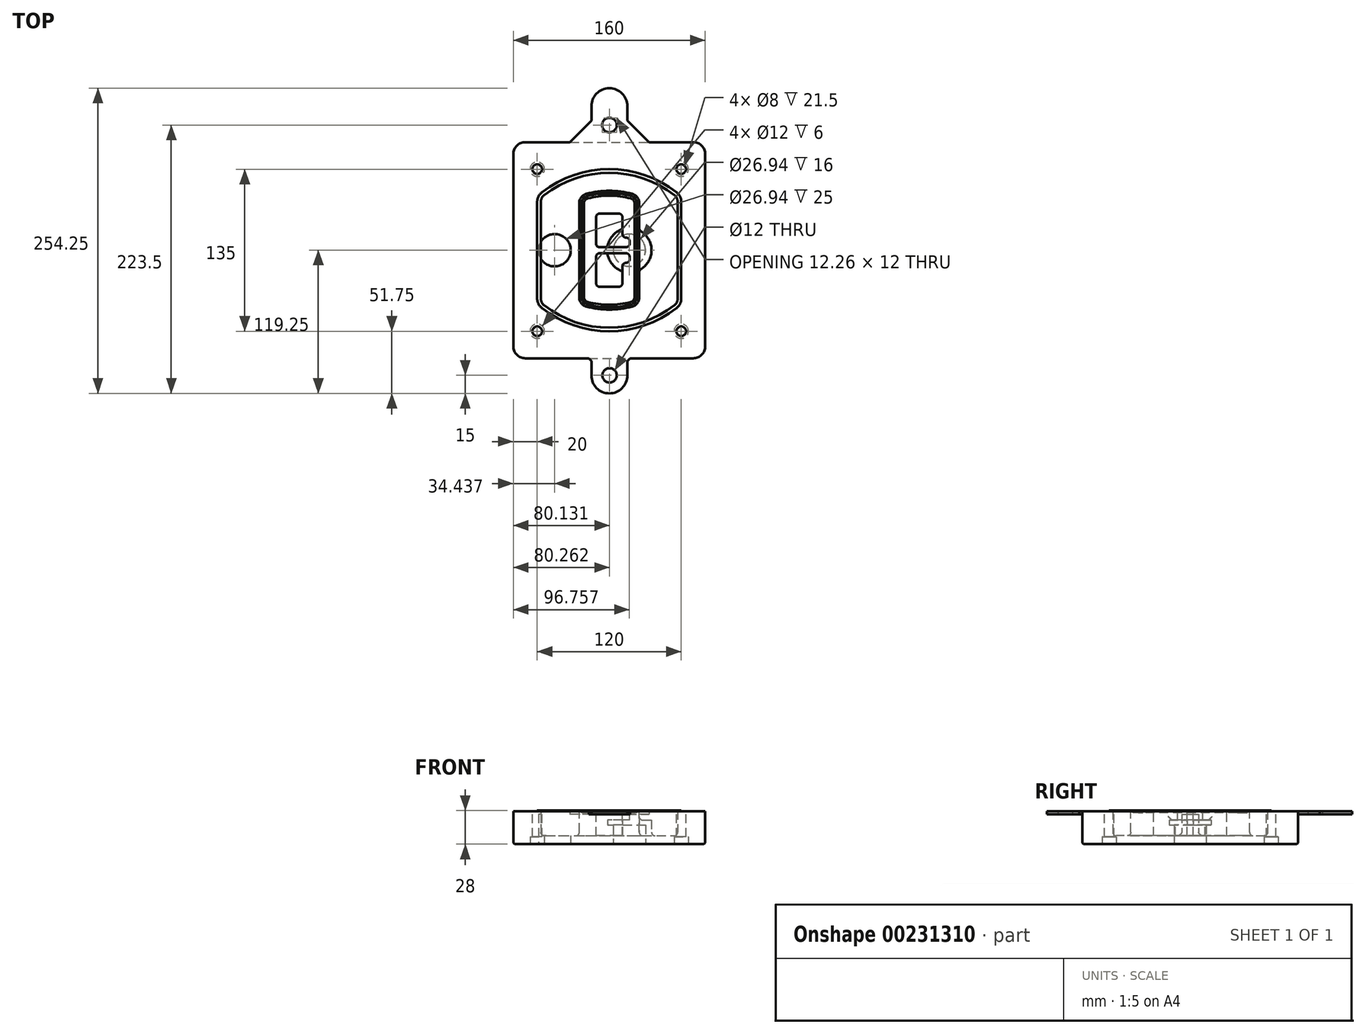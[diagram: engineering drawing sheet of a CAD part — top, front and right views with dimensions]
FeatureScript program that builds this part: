
annotation { "Feature Type Name" : "Feature", "Feature Type Description" : "" }
export const myFeature = defineFeature(function(context is Context, id is Id, definition is map)
    precondition{}
    {
        {
            var Q0;
            Q0=qCreatedBy(makeId("Top.planeOp"),FACE);
            var sketch = newSketch(context, id + "F0", { "sketchPlane" : qUnion([Q0])});
            skPoint(sketch, "E0.rect.middle", {"position": v(0, 0) * mm});
            skLineSegment(sketch, "E1.bottom", {"start": v(-70, -90) * mm, "end": v(70, -90) * mm});
            skLineSegment(sketch, "E1.top", {"start": v(-70, 90) * mm, "end": v(70, 90) * mm});
            skLineSegment(sketch, "E1.left", {"start": v(-80, -80) * mm, "end": v(-80, 80) * mm});
            skLineSegment(sketch, "E1.right", {"start": v(80, -80) * mm, "end": v(80, 80) * mm});
            skLineSegment(sketch, "E2", {"start": v(-80, 90) * mm, "end": v(80, -90) * mm, "construction": true});
            skLineSegment(sketch, "E3", {"start": v(80, 90) * mm, "end": v(-80, -90) * mm, "construction": true});
            skCircle(sketch, "E4", {"center": v(-60, 67.5) * mm, "radius": 4 * mm});
            skCircle(sketch, "E5", {"center": v(60, 67.5) * mm, "radius": 4 * mm});
            skCircle(sketch, "E6", {"center": v(60, -67.5) * mm, "radius": 4 * mm});
            skCircle(sketch, "E7", {"center": v(-60, -67.5) * mm, "radius": 4 * mm});
            skLineSegment(sketch, "E8", {"start": v(-60, 67.5) * mm, "end": v(60, 67.5) * mm, "construction": true});
            skLineSegment(sketch, "E9", {"start": v(60, 67.5) * mm, "end": v(60, -67.5) * mm, "construction": true});
            skLineSegment(sketch, "E10", {"start": v(60, -67.5) * mm, "end": v(-60, -67.5) * mm, "construction": true});
            skLineSegment(sketch, "E11", {"start": v(-60, -67.5) * mm, "end": v(-60, 67.5) * mm, "construction": true});
            skLineSegment(sketch, "E12", {"start": v(-60, 40.3) * mm, "end": v(-60, -40.3) * mm});
            skLineSegment(sketch, "E13", {"start": v(60, 40.3) * mm, "end": v(60, -40.3) * mm});
            skArc(sketch, "E14", {"start": v(56.15, 48.18) * mm, "mid": v(0, 67.5) * mm, "end": v(-56.15, 48.18) * mm});
            skArc(sketch, "E15", {"start": v(-56.15, -48.18) * mm, "mid": v(0, -67.5) * mm, "end": v(56.15, -48.18) * mm});
            skLineSegment(sketch, "E16", {"start": v(-60, 0) * mm, "end": v(60, 0) * mm, "construction": true});
            skPoint(sketch, "E17.visualSharp", {"position": v(-60, -45) * mm});
            skArc(sketch, "E17.filletArc", {"start": v(-60, -40.3) * mm, "mid": v(-58.99, -44.68) * mm, "end": v(-56.15, -48.18) * mm});
            skPoint(sketch, "E18.visualSharp", {"position": v(-60, 45) * mm});
            skArc(sketch, "E18.filletArc", {"start": v(-56.15, 48.18) * mm, "mid": v(-58.99, 44.68) * mm, "end": v(-60, 40.3) * mm});
            skPoint(sketch, "E19.visualSharp", {"position": v(60, 45) * mm});
            skArc(sketch, "E19.filletArc", {"start": v(60, 40.3) * mm, "mid": v(58.99, 44.68) * mm, "end": v(56.15, 48.18) * mm});
            skPoint(sketch, "E20.visualSharp", {"position": v(60, -45) * mm});
            skArc(sketch, "E20.filletArc", {"start": v(56.15, -48.18) * mm, "mid": v(58.99, -44.68) * mm, "end": v(60, -40.3) * mm});
            skPoint(sketch, "E21.visualSharp", {"position": v(-80, 90) * mm});
            skArc(sketch, "E21.filletArc", {"start": v(-70, 90) * mm, "mid": v(-77.07, 87.07) * mm, "end": v(-80, 80) * mm});
            skPoint(sketch, "E22.visualSharp", {"position": v(80, 90) * mm});
            skArc(sketch, "E22.filletArc", {"start": v(80, 80) * mm, "mid": v(77.07, 87.07) * mm, "end": v(70, 90) * mm});
            skPoint(sketch, "E23.visualSharp", {"position": v(80, -90) * mm});
            skArc(sketch, "E23.filletArc", {"start": v(70, -90) * mm, "mid": v(77.07, -87.07) * mm, "end": v(80, -80) * mm});
            skPoint(sketch, "E24.visualSharp", {"position": v(-80, -90) * mm});
            skArc(sketch, "E24.filletArc", {"start": v(-80, -80) * mm, "mid": v(-77.07, -87.07) * mm, "end": v(-70, -90) * mm});
            skArc(sketch, "E25.0", {"start": v(57, 40.3) * mm, "mid": v(56.3, 43.36) * mm, "end": v(54.3, 45.81) * mm});
            skLineSegment(sketch, "E25.1", {"start": v(57, 40.3) * mm, "end": v(57, -40.3) * mm});
            skArc(sketch, "E25.2", {"start": v(54.3, -45.81) * mm, "mid": v(56.3, -43.36) * mm, "end": v(57, -40.3) * mm});
            skArc(sketch, "E25.3", {"start": v(-54.3, -45.81) * mm, "mid": v(0, -64.5) * mm, "end": v(54.3, -45.81) * mm});
            skArc(sketch, "E25.4", {"start": v(-57, -40.3) * mm, "mid": v(-56.3, -43.36) * mm, "end": v(-54.3, -45.81) * mm});
            skArc(sketch, "E25.5", {"start": v(54.3, 45.81) * mm, "mid": v(0, 64.5) * mm, "end": v(-54.3, 45.81) * mm});
            skLineSegment(sketch, "E25.6", {"start": v(-57, 40.3) * mm, "end": v(-57, -40.3) * mm});
            skArc(sketch, "E25.7", {"start": v(-54.3, 45.81) * mm, "mid": v(-56.3, 43.36) * mm, "end": v(-57, 40.3) * mm});
            skArc(sketch, "E26.0", {"start": v(-58.62, 51.33) * mm, "mid": v(-62.58, 46.43) * mm, "end": v(-64, 40.3) * mm});
            skArc(sketch, "E26.1", {"start": v(58.62, 51.33) * mm, "mid": v(0, 71.5) * mm, "end": v(-58.62, 51.33) * mm});
            skArc(sketch, "E26.2", {"start": v(64, 40.3) * mm, "mid": v(62.58, 46.43) * mm, "end": v(58.62, 51.33) * mm});
            skLineSegment(sketch, "E26.3", {"start": v(64, 40.3) * mm, "end": v(64, -40.3) * mm});
            skArc(sketch, "E26.4", {"start": v(58.62, -51.33) * mm, "mid": v(62.58, -46.43) * mm, "end": v(64, -40.3) * mm});
            skLineSegment(sketch, "E26.5", {"start": v(-64, 40.3) * mm, "end": v(-64, -40.3) * mm});
            skArc(sketch, "E26.6", {"start": v(-58.62, -51.33) * mm, "mid": v(0, -71.5) * mm, "end": v(58.62, -51.33) * mm});
            skArc(sketch, "E26.7", {"start": v(-64, -40.3) * mm, "mid": v(-62.58, -46.43) * mm, "end": v(-58.62, -51.33) * mm});
            skSolve(sketch);
        }
        {
            var Q0;
            Q0=makeQuery(id+"F0.imprint","IMPRINT",FACE,{"disambiguationData":[TD([[makeQuery(id+"F0.imprint","IMPRINT",EDGE,{"derivedFrom":sQuery(id+"F0.wireOp",EDGE,"E1.bottom")}),1.0]])]});
            var Q1;
            Q1=makeQuery(id+"F0.imprint","IMPRINT",FACE,{"disambiguationData":[TD([[makeQuery(id+"F0.imprint","IMPRINT",EDGE,{"derivedFrom":sQuery(id+"F0.wireOp",EDGE,"E12")}),1.0]])]});
            var Q2;
            Q2=makeQuery(id+"F0.imprint","IMPRINT",FACE,{"disambiguationData":[TD([[makeQuery(id+"F0.imprint","IMPRINT",EDGE,{"derivedFrom":sQuery(id+"F0.wireOp",EDGE,"E25.0")}),1.0]])]});
            var Q3;
            Q3=makeQuery(id+"F0.imprint","IMPRINT",FACE,{"disambiguationData":[TD([[makeQuery(id+"F0.imprint","IMPRINT",EDGE,{"derivedFrom":sQuery(id+"F0.wireOp",EDGE,"E12")}),-1.0]])]});
            extrude(context, id + "F1", {"entities" : qUnion([Q0, Q1, Q2, Q3]), "oppositeDirection" : true, "depth" : 25 * mm});
        }
        {
            var Q0;
            Q0=makeQuery(id+"F0.imprint","IMPRINT",FACE,{"disambiguationData":[TD([[makeQuery(id+"F0.imprint","IMPRINT",EDGE,{"derivedFrom":sQuery(id+"F0.wireOp",EDGE,"E12")}),1.0]])]});
            extrude(context, id + "F2", {"entities" : qUnion([Q0]), "operationType" : NewBodyOperationType.ADD, "depth" : 3 * mm});
        }
        {
            var Q0;
            Q0=makeQuery(id+"F0.imprint","IMPRINT",FACE,{"disambiguationData":[TD([[makeQuery(id+"F0.imprint","IMPRINT",EDGE,{"derivedFrom":sQuery(id+"F0.wireOp",EDGE,"E25.0")}),1.0]])]});
            extrude(context, id + "F3", {"entities" : qUnion([Q0]), "operationType" : NewBodyOperationType.REMOVE, "oppositeDirection" : true, "depth" : 18 * mm});
        }
        {
            var Q0;
            Q0=makeQuery(id+"F2.opExtrude","CAP_FACE",FACE,{"disambiguationData":[OSD([sQuery(id+"F0.wireOp",EDGE,"E12"),sQuery(id+"F0.wireOp",EDGE,"E13"),sQuery(id+"F0.wireOp",EDGE,"E14"),sQuery(id+"F0.wireOp",EDGE,"E15"),sQuery(id+"F0.wireOp",EDGE,"E17.filletArc"),sQuery(id+"F0.wireOp",EDGE,"E18.filletArc"),sQuery(id+"F0.wireOp",EDGE,"E19.filletArc"),sQuery(id+"F0.wireOp",EDGE,"E20.filletArc"),sQuery(id+"F0.wireOp",EDGE,"E25.0"),sQuery(id+"F0.wireOp",EDGE,"E25.1"),sQuery(id+"F0.wireOp",EDGE,"E25.2"),sQuery(id+"F0.wireOp",EDGE,"E25.3"),sQuery(id+"F0.wireOp",EDGE,"E25.4"),sQuery(id+"F0.wireOp",EDGE,"E25.5"),sQuery(id+"F0.wireOp",EDGE,"E25.6"),sQuery(id+"F0.wireOp",EDGE,"E25.7")])],"isStart":false});
            var sketch = newSketch(context, id + "F4", { "sketchPlane" : qUnion([Q0])});
            skArc(sketch, "E27.0", {"start": v(-19.08, -46.97) * mm, "mid": v(0, -49.5) * mm, "end": v(19.08, -46.97) * mm});
            skArc(sketch, "E28.0", {"start": v(19.08, 46.97) * mm, "mid": v(0, 49.5) * mm, "end": v(-19.08, 46.97) * mm});
            skLineSegment(sketch, "E29", {"start": v(-25, 39.25) * mm, "end": v(-25, -39.25) * mm});
            skLineSegment(sketch, "E30", {"start": v(25, 39.25) * mm, "end": v(25, -39.25) * mm});
            skLineSegment(sketch, "E31", {"start": v(-25, 45.1) * mm, "end": v(25, 45.1) * mm, "construction": true});
            skLineSegment(sketch, "E32", {"start": v(-25, -45.1) * mm, "end": v(25, -45.1) * mm, "construction": true});
            skPoint(sketch, "E33.visualSharp", {"position": v(-25, 45.1) * mm});
            skArc(sketch, "E33.filletArc", {"start": v(-19.08, 46.97) * mm, "mid": v(-23.35, 44.11) * mm, "end": v(-25, 39.25) * mm});
            skPoint(sketch, "E34.visualSharp", {"position": v(25, 45.1) * mm});
            skArc(sketch, "E34.filletArc", {"start": v(25, 39.25) * mm, "mid": v(23.35, 44.11) * mm, "end": v(19.08, 46.97) * mm});
            skPoint(sketch, "E35.visualSharp", {"position": v(25, -45.1) * mm});
            skArc(sketch, "E35.filletArc", {"start": v(19.08, -46.97) * mm, "mid": v(23.35, -44.11) * mm, "end": v(25, -39.25) * mm});
            skPoint(sketch, "E36.visualSharp", {"position": v(-25, -45.1) * mm});
            skArc(sketch, "E36.filletArc", {"start": v(-25, -39.25) * mm, "mid": v(-23.35, -44.11) * mm, "end": v(-19.08, -46.97) * mm});
            skArc(sketch, "E37.0", {"start": v(54.3, 45.81) * mm, "mid": v(0, 64.5) * mm, "end": v(-54.3, 45.81) * mm});
            skArc(sketch, "E37.1", {"start": v(-54.3, 45.81) * mm, "mid": v(-56.3, 43.36) * mm, "end": v(-57, 40.3) * mm});
            skLineSegment(sketch, "E37.2", {"start": v(-57, 40.3) * mm, "end": v(-57, -40.3) * mm});
            skArc(sketch, "E37.3", {"start": v(-57, -40.3) * mm, "mid": v(-56.3, -43.36) * mm, "end": v(-54.3, -45.81) * mm});
            skArc(sketch, "E37.4", {"start": v(-54.3, -45.81) * mm, "mid": v(0, -64.5) * mm, "end": v(54.3, -45.81) * mm});
            skArc(sketch, "E37.5", {"start": v(54.3, -45.81) * mm, "mid": v(56.3, -43.36) * mm, "end": v(57, -40.3) * mm});
            skLineSegment(sketch, "E37.6", {"start": v(57, 40.3) * mm, "end": v(57, -40.3) * mm});
            skArc(sketch, "E37.7", {"start": v(57, 40.3) * mm, "mid": v(56.3, 43.36) * mm, "end": v(54.3, 45.81) * mm});
            skLineSegment(sketch, "E38.0", {"start": v(23, 39.25) * mm, "end": v(23, -39.25) * mm});
            skArc(sketch, "E38.1", {"start": v(18.56, -45.04) * mm, "mid": v(21.76, -42.9) * mm, "end": v(23, -39.25) * mm});
            skArc(sketch, "E38.2", {"start": v(-18.56, -45.04) * mm, "mid": v(0, -47.5) * mm, "end": v(18.56, -45.04) * mm});
            skArc(sketch, "E38.3", {"start": v(-23, -39.25) * mm, "mid": v(-21.76, -42.9) * mm, "end": v(-18.56, -45.04) * mm});
            skLineSegment(sketch, "E38.4", {"start": v(-23, 39.25) * mm, "end": v(-23, -39.25) * mm});
            skArc(sketch, "E38.5", {"start": v(23, 39.25) * mm, "mid": v(21.76, 42.9) * mm, "end": v(18.56, 45.04) * mm});
            skArc(sketch, "E38.6", {"start": v(-18.56, 45.04) * mm, "mid": v(-21.76, 42.9) * mm, "end": v(-23, 39.25) * mm});
            skArc(sketch, "E38.7", {"start": v(18.56, 45.04) * mm, "mid": v(0, 47.5) * mm, "end": v(-18.56, 45.04) * mm});
            skArc(sketch, "E39.0", {"start": v(21, 39.25) * mm, "mid": v(20.18, 41.68) * mm, "end": v(18.04, 43.1) * mm});
            skLineSegment(sketch, "E39.1", {"start": v(21, 39.25) * mm, "end": v(21, -39.25) * mm});
            skArc(sketch, "E39.2", {"start": v(18.04, -43.1) * mm, "mid": v(20.18, -41.68) * mm, "end": v(21, -39.25) * mm});
            skArc(sketch, "E39.3", {"start": v(-18.04, -43.1) * mm, "mid": v(0, -45.5) * mm, "end": v(18.04, -43.1) * mm});
            skArc(sketch, "E39.4", {"start": v(-21, -39.25) * mm, "mid": v(-20.18, -41.68) * mm, "end": v(-18.04, -43.1) * mm});
            skArc(sketch, "E39.5", {"start": v(18.04, 43.1) * mm, "mid": v(0, 45.5) * mm, "end": v(-18.04, 43.1) * mm});
            skLineSegment(sketch, "E39.6", {"start": v(-21, 39.25) * mm, "end": v(-21, -39.25) * mm});
            skArc(sketch, "E39.7", {"start": v(-18.04, 43.1) * mm, "mid": v(-20.18, 41.68) * mm, "end": v(-21, 39.25) * mm});
            skLineSegment(sketch, "E40", {"start": v(-25, 0) * mm, "end": v(25, 0) * mm, "construction": true});
            skLineSegment(sketch, "E41", {"start": v(-11, 5.5) * mm, "end": v(-11, 27.5) * mm});
            skLineSegment(sketch, "E42", {"start": v(-8, 30.5) * mm, "end": v(8, 30.5) * mm});
            skLineSegment(sketch, "E43", {"start": v(11, 27.5) * mm, "end": v(11, 13.5) * mm});
            skLineSegment(sketch, "E44", {"start": v(14, 10.5) * mm, "end": v(14, 10.5) * mm});
            skLineSegment(sketch, "E45", {"start": v(17, 7.5) * mm, "end": v(17, 5.5) * mm});
            skLineSegment(sketch, "E46", {"start": v(14, 2.5) * mm, "end": v(-8, 2.5) * mm});
            skPoint(sketch, "E47.visualSharp", {"position": v(-11, 30.5) * mm});
            skArc(sketch, "E47.filletArc", {"start": v(-8, 30.5) * mm, "mid": v(-10.12, 29.62) * mm, "end": v(-11, 27.5) * mm});
            skPoint(sketch, "E48.visualSharp", {"position": v(11, 30.5) * mm});
            skArc(sketch, "E48.filletArc", {"start": v(11, 27.5) * mm, "mid": v(10.12, 29.62) * mm, "end": v(8, 30.5) * mm});
            skPoint(sketch, "E49.visualSharp", {"position": v(11, 10.5) * mm});
            skArc(sketch, "E49.filletArc", {"start": v(11, 13.5) * mm, "mid": v(11.88, 11.38) * mm, "end": v(14, 10.5) * mm});
            skPoint(sketch, "E50.visualSharp", {"position": v(17, 10.5) * mm});
            skArc(sketch, "E50.filletArc", {"start": v(17, 7.5) * mm, "mid": v(16.12, 9.62) * mm, "end": v(14, 10.5) * mm});
            skPoint(sketch, "E51.visualSharp", {"position": v(17, 2.5) * mm});
            skArc(sketch, "E51.filletArc", {"start": v(14, 2.5) * mm, "mid": v(16.12, 3.38) * mm, "end": v(17, 5.5) * mm});
            skPoint(sketch, "E52.visualSharp", {"position": v(-11, 2.5) * mm});
            skArc(sketch, "E52.filletArc", {"start": v(-11, 5.5) * mm, "mid": v(-10.12, 3.38) * mm, "end": v(-8, 2.5) * mm});
            skLineSegment(sketch, "E53.0.MirrorCS", {"start": v(14, -2.5) * mm, "end": v(-8, -2.5) * mm});
            skArc(sketch, "E54.0.MirrorCS", {"start": v(-11, -5.5) * mm, "mid": v(-10.12, -3.38) * mm, "end": v(-8, -2.5) * mm});
            skLineSegment(sketch, "E55.0.MirrorCS", {"start": v(-11, -5.5) * mm, "end": v(-11, -27.5) * mm});
            skArc(sketch, "E56.0.MirrorCS", {"start": v(-8, -30.5) * mm, "mid": v(-10.12, -29.62) * mm, "end": v(-11, -27.5) * mm});
            skLineSegment(sketch, "E57.0.MirrorCS", {"start": v(-8, -30.5) * mm, "end": v(8, -30.5) * mm});
            skArc(sketch, "E58.0.MirrorCS", {"start": v(11, -27.5) * mm, "mid": v(10.12, -29.62) * mm, "end": v(8, -30.5) * mm});
            skLineSegment(sketch, "E59.0.MirrorCS", {"start": v(11, -27.5) * mm, "end": v(11, -13.5) * mm});
            skArc(sketch, "E60.0.MirrorCS", {"start": v(11, -13.5) * mm, "mid": v(11.88, -11.38) * mm, "end": v(14, -10.5) * mm});
            skArc(sketch, "E61.0.MirrorCS", {"start": v(17, -7.5) * mm, "mid": v(16.12, -9.62) * mm, "end": v(14, -10.5) * mm});
            skLineSegment(sketch, "E62.0.MirrorCS", {"start": v(17, -7.5) * mm, "end": v(17, -5.5) * mm});
            skArc(sketch, "E63.0.MirrorCS", {"start": v(14, -2.5) * mm, "mid": v(16.12, -3.38) * mm, "end": v(17, -5.5) * mm});
            skSolve(sketch);
        }
        {
            var Q0;
            Q0=makeQuery(id+"F4.imprint","IMPRINT",FACE,{"disambiguationData":[TD([[makeQuery(id+"F4.imprint","IMPRINT",EDGE,{"derivedFrom":sQuery(id+"F4.wireOp",EDGE,"E27.0")}),1.0]])]});
            var Q1;
            Q1=makeQuery(id+"F4.imprint","IMPRINT",FACE,{"disambiguationData":[TD([[makeQuery(id+"F4.imprint","IMPRINT",EDGE,{"derivedFrom":sQuery(id+"F4.wireOp",EDGE,"E38.0")}),-1.0]])]});
            var Q2;
            Q2=makeQuery(id+"F4.imprint","IMPRINT",FACE,{"disambiguationData":[TD([[makeQuery(id+"F4.imprint","IMPRINT",EDGE,{"derivedFrom":sQuery(id+"F4.wireOp",EDGE,"E39.0")}),1.0]])]});
            extrude(context, id + "F5", {"entities" : qUnion([Q0, Q1, Q2]), "operationType" : NewBodyOperationType.ADD, "endBound" : BoundingType.UP_TO_NEXT, "oppositeDirection" : true, "depth" : 25 * mm});
        }
        {
            var Q0;
            Q0=makeQuery(id+"F4.imprint","IMPRINT",FACE,{"disambiguationData":[TD([[makeQuery(id+"F4.imprint","IMPRINT",EDGE,{"derivedFrom":sQuery(id+"F4.wireOp",EDGE,"E38.0")}),-1.0]])]});
            extrude(context, id + "F6", {"entities" : qUnion([Q0]), "operationType" : NewBodyOperationType.REMOVE, "oppositeDirection" : true, "depth" : 2 * mm});
        }
        {
            var Q0;
            Q0=makeQuery(id+"F1.opExtrude","CAP_FACE",FACE,{"disambiguationData":[OSD([sQuery(id+"F0.wireOp",EDGE,"E1.bottom"),sQuery(id+"F0.wireOp",EDGE,"E1.top"),sQuery(id+"F0.wireOp",EDGE,"E1.left"),sQuery(id+"F0.wireOp",EDGE,"E1.right"),sQuery(id+"F0.wireOp",EDGE,"E4"),sQuery(id+"F0.wireOp",EDGE,"E5"),sQuery(id+"F0.wireOp",EDGE,"E6"),sQuery(id+"F0.wireOp",EDGE,"E7"),sQuery(id+"F0.wireOp",EDGE,"E21.filletArc"),sQuery(id+"F0.wireOp",EDGE,"E22.filletArc"),sQuery(id+"F0.wireOp",EDGE,"E23.filletArc"),sQuery(id+"F0.wireOp",EDGE,"E24.filletArc")])],"isStart":false});
            var sketch = newSketch(context, id + "F7", { "sketchPlane" : qUnion([Q0])});
            skCircle(sketch, "E64", {"center": v(16.76, 0) * mm, "radius": 13.47 * mm});
            skCircle(sketch, "E65", {"center": v(-45.56, 0) * mm, "radius": 13.47 * mm});
            skLineSegment(sketch, "E66", {"start": v(80, 0) * mm, "end": v(-80, 0) * mm});
            skCircle(sketch, "E67", {"center": v(16.76, 0) * mm, "radius": 18.47 * mm});
            skCircle(sketch, "E68", {"center": v(60, -67.5) * mm, "radius": 6 * mm});
            skCircle(sketch, "E69", {"center": v(-60, -67.5) * mm, "radius": 6 * mm});
            skCircle(sketch, "E70", {"center": v(-60, 67.5) * mm, "radius": 6 * mm});
            skCircle(sketch, "E71", {"center": v(60, 67.5) * mm, "radius": 6 * mm});
            skSolve(sketch);
        }
        {
            var Q0;
            {var subQ1=sQuery(id+"F7.wireOp",EDGE,"E66");var subQ4=sQuery(id+"F7.wireOp",EDGE,"E64");var subQ6=makeQuery(id+"F7.imprint","INTERSECT",VERTEX,{"disambiguationData":[OD(0.0)],"derivedFrom":[subQ4,subQ1]});Q0=makeQuery(id+"F7.imprint","IMPRINT",FACE,{"disambiguationData":[TD([[makeQuery(id+"F7.imprint","IMPRINT",EDGE,{"disambiguationData":[TD([[subQ6,-1.0]])],"derivedFrom":subQ4}),-1.0]])]});}
            var Q1;
            {var subQ0=sQuery(id+"F7.wireOp",EDGE,"E66");var subQ1=sQuery(id+"F7.wireOp",EDGE,"E64");var subQ3=makeQuery(id+"F7.imprint","INTERSECT",VERTEX,{"disambiguationData":[OD(0.0)],"derivedFrom":[subQ1,subQ0]});Q1=makeQuery(id+"F7.imprint","IMPRINT",FACE,{"disambiguationData":[TD([[makeQuery(id+"F7.imprint","IMPRINT",EDGE,{"disambiguationData":[TD([[subQ3,-1.0]])],"derivedFrom":subQ1}),1.0]])]});}
            var Q2;
            {var subQ0=sQuery(id+"F7.wireOp",EDGE,"E66");var subQ1=sQuery(id+"F7.wireOp",EDGE,"E64");var subQ3=makeQuery(id+"F7.imprint","INTERSECT",VERTEX,{"disambiguationData":[OD(0.0)],"derivedFrom":[subQ1,subQ0]});Q2=makeQuery(id+"F7.imprint","IMPRINT",FACE,{"disambiguationData":[TD([[makeQuery(id+"F7.imprint","IMPRINT",EDGE,{"disambiguationData":[TD([[subQ3,1.0]])],"derivedFrom":subQ1}),1.0]])]});}
            var Q3;
            {var subQ1=sQuery(id+"F7.wireOp",EDGE,"E66");var subQ4=sQuery(id+"F7.wireOp",EDGE,"E64");var subQ6=makeQuery(id+"F7.imprint","INTERSECT",VERTEX,{"disambiguationData":[OD(0.0)],"derivedFrom":[subQ4,subQ1]});Q3=makeQuery(id+"F7.imprint","IMPRINT",FACE,{"disambiguationData":[TD([[makeQuery(id+"F7.imprint","IMPRINT",EDGE,{"disambiguationData":[TD([[subQ6,1.0]])],"derivedFrom":subQ4}),-1.0]])]});}
            extrude(context, id + "F8", {"entities" : qUnion([Q0, Q1, Q2, Q3]), "operationType" : NewBodyOperationType.ADD, "oppositeDirection" : true, "depth" : 20 * mm});
        }
        {
            var Q0;
            {var subQ0=sQuery(id+"F7.wireOp",EDGE,"E66");var subQ1=sQuery(id+"F7.wireOp",EDGE,"E64");var subQ3=makeQuery(id+"F7.imprint","INTERSECT",VERTEX,{"disambiguationData":[OD(0.0)],"derivedFrom":[subQ1,subQ0]});Q0=makeQuery(id+"F7.imprint","IMPRINT",FACE,{"disambiguationData":[TD([[makeQuery(id+"F7.imprint","IMPRINT",EDGE,{"disambiguationData":[TD([[subQ3,-1.0]])],"derivedFrom":subQ1}),1.0]])]});}
            var Q1;
            {var subQ0=sQuery(id+"F7.wireOp",EDGE,"E66");var subQ1=sQuery(id+"F7.wireOp",EDGE,"E64");var subQ3=makeQuery(id+"F7.imprint","INTERSECT",VERTEX,{"disambiguationData":[OD(0.0)],"derivedFrom":[subQ1,subQ0]});Q1=makeQuery(id+"F7.imprint","IMPRINT",FACE,{"disambiguationData":[TD([[makeQuery(id+"F7.imprint","IMPRINT",EDGE,{"disambiguationData":[TD([[subQ3,1.0]])],"derivedFrom":subQ1}),1.0]])]});}
            extrude(context, id + "F9", {"entities" : qUnion([Q0, Q1]), "operationType" : NewBodyOperationType.REMOVE, "oppositeDirection" : true, "depth" : 16 * mm});
        }
        {
            var Q0;
            {var subQ0=sQuery(id+"F7.wireOp",EDGE,"E66");var subQ1=sQuery(id+"F7.wireOp",EDGE,"E65");var subQ3=makeQuery(id+"F7.imprint","INTERSECT",VERTEX,{"disambiguationData":[OD(0.0)],"derivedFrom":[subQ1,subQ0]});Q0=makeQuery(id+"F7.imprint","IMPRINT",FACE,{"disambiguationData":[TD([[makeQuery(id+"F7.imprint","IMPRINT",EDGE,{"disambiguationData":[TD([[subQ3,-1.0]])],"derivedFrom":subQ1}),1.0]])]});}
            var Q1;
            {var subQ0=sQuery(id+"F7.wireOp",EDGE,"E66");var subQ1=sQuery(id+"F7.wireOp",EDGE,"E65");var subQ3=makeQuery(id+"F7.imprint","INTERSECT",VERTEX,{"disambiguationData":[OD(0.0)],"derivedFrom":[subQ1,subQ0]});Q1=makeQuery(id+"F7.imprint","IMPRINT",FACE,{"disambiguationData":[TD([[makeQuery(id+"F7.imprint","IMPRINT",EDGE,{"disambiguationData":[TD([[subQ3,1.0]])],"derivedFrom":subQ1}),1.0]])]});}
            extrude(context, id + "F10", {"entities" : qUnion([Q0, Q1]), "operationType" : NewBodyOperationType.REMOVE, "oppositeDirection" : true, "depth" : 25 * mm});
        }
        {
            var Q0;
            Q0=makeQuery(id+"F7.imprint","IMPRINT",FACE,{"disambiguationData":[TD([[makeQuery(id+"F7.imprint","IMPRINT",EDGE,{"derivedFrom":sQuery(id+"F7.wireOp",EDGE,"E68")}),1.0]])]});
            var Q1;
            Q1=makeQuery(id+"F7.imprint","IMPRINT",FACE,{"disambiguationData":[TD([[makeQuery(id+"F7.imprint","IMPRINT",EDGE,{"derivedFrom":makeQuery(id+"F1.opExtrude","CAP_EDGE",EDGE,{"disambiguationData":[OSD([sQuery(id+"F0.wireOp",EDGE,"E5")])],"isStart":false})}),-1.0]])]});
            var Q2;
            Q2=makeQuery(id+"F7.imprint","IMPRINT",FACE,{"disambiguationData":[TD([[makeQuery(id+"F7.imprint","IMPRINT",EDGE,{"derivedFrom":sQuery(id+"F7.wireOp",EDGE,"E69")}),1.0]])]});
            var Q3;
            Q3=makeQuery(id+"F7.imprint","IMPRINT",FACE,{"disambiguationData":[TD([[makeQuery(id+"F7.imprint","IMPRINT",EDGE,{"derivedFrom":makeQuery(id+"F1.opExtrude","CAP_EDGE",EDGE,{"disambiguationData":[OSD([sQuery(id+"F0.wireOp",EDGE,"E4")])],"isStart":false})}),-1.0]])]});
            var Q4;
            Q4=makeQuery(id+"F7.imprint","IMPRINT",FACE,{"disambiguationData":[TD([[makeQuery(id+"F7.imprint","IMPRINT",EDGE,{"derivedFrom":sQuery(id+"F7.wireOp",EDGE,"E70")}),1.0]])]});
            var Q5;
            Q5=makeQuery(id+"F7.imprint","IMPRINT",FACE,{"disambiguationData":[TD([[makeQuery(id+"F7.imprint","IMPRINT",EDGE,{"derivedFrom":makeQuery(id+"F1.opExtrude","CAP_EDGE",EDGE,{"disambiguationData":[OSD([sQuery(id+"F0.wireOp",EDGE,"E7")])],"isStart":false})}),-1.0]])]});
            var Q6;
            Q6=makeQuery(id+"F7.imprint","IMPRINT",FACE,{"disambiguationData":[TD([[makeQuery(id+"F7.imprint","IMPRINT",EDGE,{"derivedFrom":sQuery(id+"F7.wireOp",EDGE,"E71")}),1.0]])]});
            var Q7;
            Q7=makeQuery(id+"F7.imprint","IMPRINT",FACE,{"disambiguationData":[TD([[makeQuery(id+"F7.imprint","IMPRINT",EDGE,{"derivedFrom":makeQuery(id+"F1.opExtrude","CAP_EDGE",EDGE,{"disambiguationData":[OSD([sQuery(id+"F0.wireOp",EDGE,"E6")])],"isStart":false})}),-1.0]])]});
            extrude(context, id + "F11", {"entities" : qUnion([Q0, Q1, Q2, Q3, Q4, Q5, Q6, Q7]), "operationType" : NewBodyOperationType.REMOVE, "oppositeDirection" : true, "depth" : 6 * mm});
        }
        {
            var Q0;
            Q0=makeQuery(id+"F9.boolean.opBoolean","COPY",FACE,{"derivedFrom":makeQuery(id+"F9.opExtrude","CAP_FACE",FACE,{"disambiguationData":[OSD([sQuery(id+"F7.wireOp",EDGE,"E64")])],"isStart":false})});
            var sketch = newSketch(context, id + "F12", { "sketchPlane" : qUnion([Q0])});
            skArc(sketch, "E72.0", {"start": v(11, 17.55) * mm, "mid": v(2.57, 11.82) * mm, "end": v(-1.54, 2.5) * mm});
            skArc(sketch, "E72.1", {"start": v(-1.54, -2.5) * mm, "mid": v(2.57, -11.82) * mm, "end": v(11, -17.55) * mm});
            skLineSegment(sketch, "E73", {"start": v(-1.54, -2.5) * mm, "end": v(14, -2.5) * mm});
            skLineSegment(sketch, "E74.0", {"start": v(14, 2.5) * mm, "end": v(-1.54, 2.5) * mm});
            skArc(sketch, "E74.1", {"start": v(14, 2.5) * mm, "mid": v(16.12, 3.38) * mm, "end": v(17, 5.5) * mm});
            skLineSegment(sketch, "E74.2", {"start": v(17, 7.5) * mm, "end": v(17, 5.5) * mm});
            skArc(sketch, "E74.3", {"start": v(17, 7.5) * mm, "mid": v(16.12, 9.62) * mm, "end": v(14, 10.5) * mm});
            skArc(sketch, "E74.4", {"start": v(11, 13.5) * mm, "mid": v(11.88, 11.38) * mm, "end": v(14, 10.5) * mm});
            skLineSegment(sketch, "E74.5", {"start": v(11, 17.55) * mm, "end": v(11, 13.5) * mm});
            skLineSegment(sketch, "E74.7", {"start": v(14, -2.5) * mm, "end": v(-1.54, -2.5) * mm});
            skArc(sketch, "E74.8", {"start": v(14, -2.5) * mm, "mid": v(16.12, -3.38) * mm, "end": v(17, -5.5) * mm});
            skLineSegment(sketch, "E74.9", {"start": v(17, -7.5) * mm, "end": v(17, -5.5) * mm});
            skArc(sketch, "E74.10", {"start": v(17, -7.5) * mm, "mid": v(16.12, -9.62) * mm, "end": v(14, -10.5) * mm});
            skArc(sketch, "E74.11", {"start": v(11, -13.5) * mm, "mid": v(11.88, -11.38) * mm, "end": v(14, -10.5) * mm});
            skLineSegment(sketch, "E74.12", {"start": v(11, -17.55) * mm, "end": v(11, -13.5) * mm});
            skPoint(sketch, "E75.orphan", {"position": v(11, -27.5) * mm});
            skPoint(sketch, "E76.orphan", {"position": v(-8, -2.5) * mm});
            skPoint(sketch, "E77.orphan", {"position": v(-8, 2.5) * mm});
            skPoint(sketch, "E78.orphan", {"position": v(11, 27.5) * mm});
            skSolve(sketch);
        }
        {
            var Q0;
            {var subQ7=sQuery(id+"F12.wireOp",EDGE,"E72.0");var subQ14=sQuery(id+"F12.wireOp",EDGE,"E72.1");var subQ16=sQuery(id+"F12.wireOp",EDGE,"E74.1");var subQ18=sQuery(id+"F12.wireOp",EDGE,"E74.8");Q0=qUnion([makeQuery(id+"F12.imprint","IMPRINT",FACE,{"disambiguationData":[TD([[makeQuery(id+"F12.imprint","IMPRINT",EDGE,{"derivedFrom":subQ7}),1.0]])]}),makeQuery(id+"F12.imprint","IMPRINT",FACE,{"disambiguationData":[TD([[makeQuery(id+"F12.imprint","IMPRINT",EDGE,{"derivedFrom":subQ14}),1.0]])]}),makeQuery(id+"F12.imprint","IMPRINT",FACE,{"disambiguationData":[TD([[makeQuery(id+"F12.imprint","IMPRINT",EDGE,{"derivedFrom":subQ16}),1.0]])]}),makeQuery(id+"F12.imprint","IMPRINT",FACE,{"disambiguationData":[TD([[makeQuery(id+"F12.imprint","IMPRINT",EDGE,{"derivedFrom":subQ18}),-1.0]])]})]);}
            var Q1;
            Q1=makeQuery(id+"F5.boolean.opBoolean","SPLIT",FACE,{"disambiguationData":[TD([makeQuery(id+"F5.opExtrude","SWEPT_FACE",FACE,{"disambiguationData":[OSD([sQuery(id+"F4.wireOp",EDGE,"E41")])]})])],"derivedFrom":makeQuery(id+"F3.boolean.opBoolean","COPY",FACE,{"derivedFrom":makeQuery(id+"F3.opExtrude","CAP_FACE",FACE,{"disambiguationData":[OSD([sQuery(id+"F0.wireOp",EDGE,"E25.0"),sQuery(id+"F0.wireOp",EDGE,"E25.1"),sQuery(id+"F0.wireOp",EDGE,"E25.2"),sQuery(id+"F0.wireOp",EDGE,"E25.3"),sQuery(id+"F0.wireOp",EDGE,"E25.4"),sQuery(id+"F0.wireOp",EDGE,"E25.5"),sQuery(id+"F0.wireOp",EDGE,"E25.6"),sQuery(id+"F0.wireOp",EDGE,"E25.7")])],"isStart":false})})});
            extrude(context, id + "F13", {"entities" : qUnion([Q0]), "operationType" : NewBodyOperationType.REMOVE, "endBound" : BoundingType.UP_TO_SURFACE, "endBoundEntityFace" : qUnion([Q1]), "depth" : 25 * mm});
        }
        {
            var Q0;
            Q0=makeQuery(id+"F3.boolean.opBoolean","COPY",EDGE,{"derivedFrom":makeQuery(id+"F3.opExtrude","CAP_EDGE",EDGE,{"disambiguationData":[OSD([sQuery(id+"F0.wireOp",EDGE,"E25.6")])],"isStart":false})});
            var Q1;
            Q1=makeQuery(id+"F8.boolean.opBoolean","INTERSECT",EDGE,{"derivedFrom":[makeQuery(id+"F5.opExtrude","SWEPT_FACE",FACE,{"disambiguationData":[OSD([sQuery(id+"F4.wireOp",EDGE,"E30")])]}),makeQuery(id+"F8.opExtrude","CAP_FACE",FACE,{"disambiguationData":[OSD([sQuery(id+"F7.wireOp",EDGE,"E67")])],"isStart":false})]});
            var Q2;
            Q2=makeQuery(id+"F8.boolean.opBoolean","INTERSECT",EDGE,{"disambiguationData":[OD(1.0)],"derivedFrom":[makeQuery(id+"F5.opExtrude","SWEPT_FACE",FACE,{"disambiguationData":[OSD([sQuery(id+"F4.wireOp",EDGE,"E30")])]}),makeQuery(id+"F8.opExtrude","SWEPT_FACE",FACE,{"disambiguationData":[OSD([sQuery(id+"F7.wireOp",EDGE,"E67")])]})]});
            var Q3;
            {var subQ0=sQuery(id+"F4.wireOp",EDGE,"E30");Q3=makeQuery(id+"F8.boolean.opBoolean","SPLIT",EDGE,{"disambiguationData":[TD([makeQuery(id+"F5.opExtrude","SWEPT_FACE",FACE,{"disambiguationData":[OSD([sQuery(id+"F4.wireOp",EDGE,"E35.filletArc")])]})])],"derivedFrom":makeQuery(id+"F5.opExtrude","CAP_EDGE",EDGE,{"disambiguationData":[OSD([subQ0])],"isStart":false})});}
            var Q4;
            {var subQ0=sQuery(id+"F0.wireOp",EDGE,"E25.7");var subQ1=sQuery(id+"F0.wireOp",EDGE,"E25.1");var subQ2=sQuery(id+"F0.wireOp",EDGE,"E25.6");var subQ3=sQuery(id+"F0.wireOp",EDGE,"E25.5");var subQ4=sQuery(id+"F0.wireOp",EDGE,"E25.4");var subQ5=sQuery(id+"F0.wireOp",EDGE,"E25.0");var subQ6=sQuery(id+"F0.wireOp",EDGE,"E25.2");var subQ7=sQuery(id+"F0.wireOp",EDGE,"E25.3");Q4=makeQuery(id+"F8.boolean.opBoolean","INTERSECT",EDGE,{"derivedFrom":[makeQuery(id+"F5.boolean.opBoolean","SPLIT",FACE,{"disambiguationData":[TD([makeQuery(id+"F2.opExtrude","SWEPT_FACE",FACE,{"disambiguationData":[OSD([subQ5])]})])],"derivedFrom":makeQuery(id+"F3.boolean.opBoolean","COPY",FACE,{"derivedFrom":makeQuery(id+"F3.opExtrude","CAP_FACE",FACE,{"disambiguationData":[OSD([subQ5,subQ1,subQ6,subQ7,subQ4,subQ3,subQ2,subQ0])],"isStart":false})})}),makeQuery(id+"F8.opExtrude","SWEPT_FACE",FACE,{"disambiguationData":[OSD([sQuery(id+"F7.wireOp",EDGE,"E67")])]})]});}
            var Q5;
            Q5=makeQuery(id+"F8.boolean.opBoolean","INTERSECT",EDGE,{"disambiguationData":[OD(0.0)],"derivedFrom":[makeQuery(id+"F5.opExtrude","SWEPT_FACE",FACE,{"disambiguationData":[OSD([sQuery(id+"F4.wireOp",EDGE,"E30")])]}),makeQuery(id+"F8.opExtrude","SWEPT_FACE",FACE,{"disambiguationData":[OSD([sQuery(id+"F7.wireOp",EDGE,"E67")])]})]});
            fillet(context, id + "F14", {"entities" : qUnion([Q0, Q1, Q2, Q3, Q4, Q5]), "radius" : 3 * mm, "tangentPropagation" : true, "allowEdgeOverflow" : false});
        }
        {
            var Q0;
            Q0=makeQuery(id+"F1.opExtrude","CAP_EDGE",EDGE,{"disambiguationData":[OSD([sQuery(id+"F0.wireOp",EDGE,"E1.bottom")])],"isStart":false});
            fillet(context, id + "F15", {"entities" : qUnion([Q0]), "radius" : 2 * mm, "tangentPropagation" : true, "allowEdgeOverflow" : false});
        }
        {
            var Q0;
            {var subQ0=sQuery(id+"F0.wireOp",EDGE,"E22.filletArc");var subQ1=sQuery(id+"F0.wireOp",EDGE,"E7");var subQ2=sQuery(id+"F0.wireOp",EDGE,"E6");var subQ3=sQuery(id+"F0.wireOp",EDGE,"E5");var subQ4=sQuery(id+"F0.wireOp",EDGE,"E4");var subQ5=sQuery(id+"F0.wireOp",EDGE,"E1.bottom");var subQ6=sQuery(id+"F0.wireOp",EDGE,"E21.filletArc");var subQ7=sQuery(id+"F0.wireOp",EDGE,"E1.top");var subQ8=sQuery(id+"F0.wireOp",EDGE,"E1.left");var subQ9=sQuery(id+"F0.wireOp",EDGE,"E1.right");var subQ10=sQuery(id+"F0.wireOp",EDGE,"E23.filletArc");var subQ11=sQuery(id+"F0.wireOp",EDGE,"E24.filletArc");Q0=makeQuery(id+"F2.boolean.opBoolean","SPLIT",FACE,{"disambiguationData":[TD([makeQuery(id+"F1.opExtrude","SWEPT_FACE",FACE,{"disambiguationData":[OSD([subQ5])]})])],"derivedFrom":makeQuery(id+"F1.opExtrude","CAP_FACE",FACE,{"disambiguationData":[OSD([subQ5,subQ7,subQ8,subQ9,subQ4,subQ3,subQ2,subQ1,subQ6,subQ0,subQ10,subQ11])],"isStart":true})});}
            var sketch = newSketch(context, id + "F16", { "sketchPlane" : qUnion([Q0])});
            skCircle(sketch, "E79", {"center": v(0, 104.25) * mm, "radius": 6 * mm});
            skLineSegment(sketch, "E80", {"start": v(-70, 90) * mm, "end": v(-63.99, 90) * mm});
            skLineSegment(sketch, "E81.trimOffspring", {"start": v(-14.87, 108) * mm, "end": v(-32.87, 90) * mm});
            skLineSegment(sketch, "E82", {"start": v(-14.87, 108) * mm, "end": v(-14.87, 120) * mm});
            skLineSegment(sketch, "E83.trimOffspring", {"start": v(15.13, 108) * mm, "end": v(33.13, 90) * mm});
            skLineSegment(sketch, "E84", {"start": v(15.13, 108) * mm, "end": v(15.13, 120) * mm});
            skArc(sketch, "E85", {"start": v(15.13, 120) * mm, "mid": v(0.13, 135) * mm, "end": v(-14.87, 120) * mm});
            skCircle(sketch, "E86.MirrorC", {"center": v(0.26, 104.25) * mm, "radius": 6 * mm});
            skArc(sketch, "E87.MirrorCS", {"start": v(-14.87, 120) * mm, "mid": v(0.13, 135) * mm, "end": v(15.13, 120) * mm});
            skLineSegment(sketch, "E88.MirrorCS", {"start": v(-14.87, 92.25) * mm, "end": v(-32.87, 74.25) * mm});
            skLineSegment(sketch, "E89.MirrorCS", {"start": v(-14.87, 92.25) * mm, "end": v(-14.87, 104.25) * mm});
            skArc(sketch, "E90.MirrorCS", {"start": v(15.13, 104.25) * mm, "mid": v(0.13, 119.25) * mm, "end": v(-14.87, 104.25) * mm});
            skLineSegment(sketch, "E91.MirrorCS", {"start": v(15.13, 92.25) * mm, "end": v(15.13, 104.25) * mm});
            skLineSegment(sketch, "E92.MirrorCS", {"start": v(70, 90) * mm, "end": v(64.51, 90) * mm});
            skLineSegment(sketch, "E93.trimOffspring", {"start": v(33.13, 90) * mm, "end": v(-32.87, 90) * mm});
            skLineSegment(sketch, "E94.trimOffspring", {"start": v(-32.87, 90) * mm, "end": v(33.13, 90) * mm});
            skLineSegment(sketch, "E95.MirrorCS", {"start": v(-14.87, -92.25) * mm, "end": v(-32.87, -74.25) * mm});
            skLineSegment(sketch, "E96.MirrorCS", {"start": v(-14.87, -92.25) * mm, "end": v(-14.87, -104.25) * mm});
            skArc(sketch, "E97.MirrorCS", {"start": v(-14.87, -104.25) * mm, "mid": v(0.13, -119.25) * mm, "end": v(15.13, -104.25) * mm});
            skCircle(sketch, "E98.MirrorC", {"center": v(0.26, -104.25) * mm, "radius": 6 * mm});
            skLineSegment(sketch, "E99.MirrorCS", {"start": v(15.13, -92.25) * mm, "end": v(15.13, -104.25) * mm});
            skLineSegment(sketch, "E100.MirrorCS", {"start": v(15.13, -92.25) * mm, "end": v(33.13, -74.25) * mm});
            skLineSegment(sketch, "E101", {"start": v(-32.87, -74.25) * mm, "end": v(33.13, -74.25) * mm});
            skSolve(sketch);
        }
        {
            var Q0;
            Q0 = qSketchRegion(id + "F16", true);
            var Q1;
            {var subQ6=sQuery(id+"F16.wireOp",EDGE,"E80");Q1=makeQuery(id+"F16.imprint","IMPRINT",FACE,{"disambiguationData":[TD([[makeQuery(id+"F16.imprint","IMPRINT",EDGE,{"derivedFrom":subQ6}),-1.0]])]});}
            extrude(context, id + "F17", {"entities" : qUnion([Q0, Q1]), "operationType" : NewBodyOperationType.ADD, "depth" : 2.5 * mm});
        }
    });
